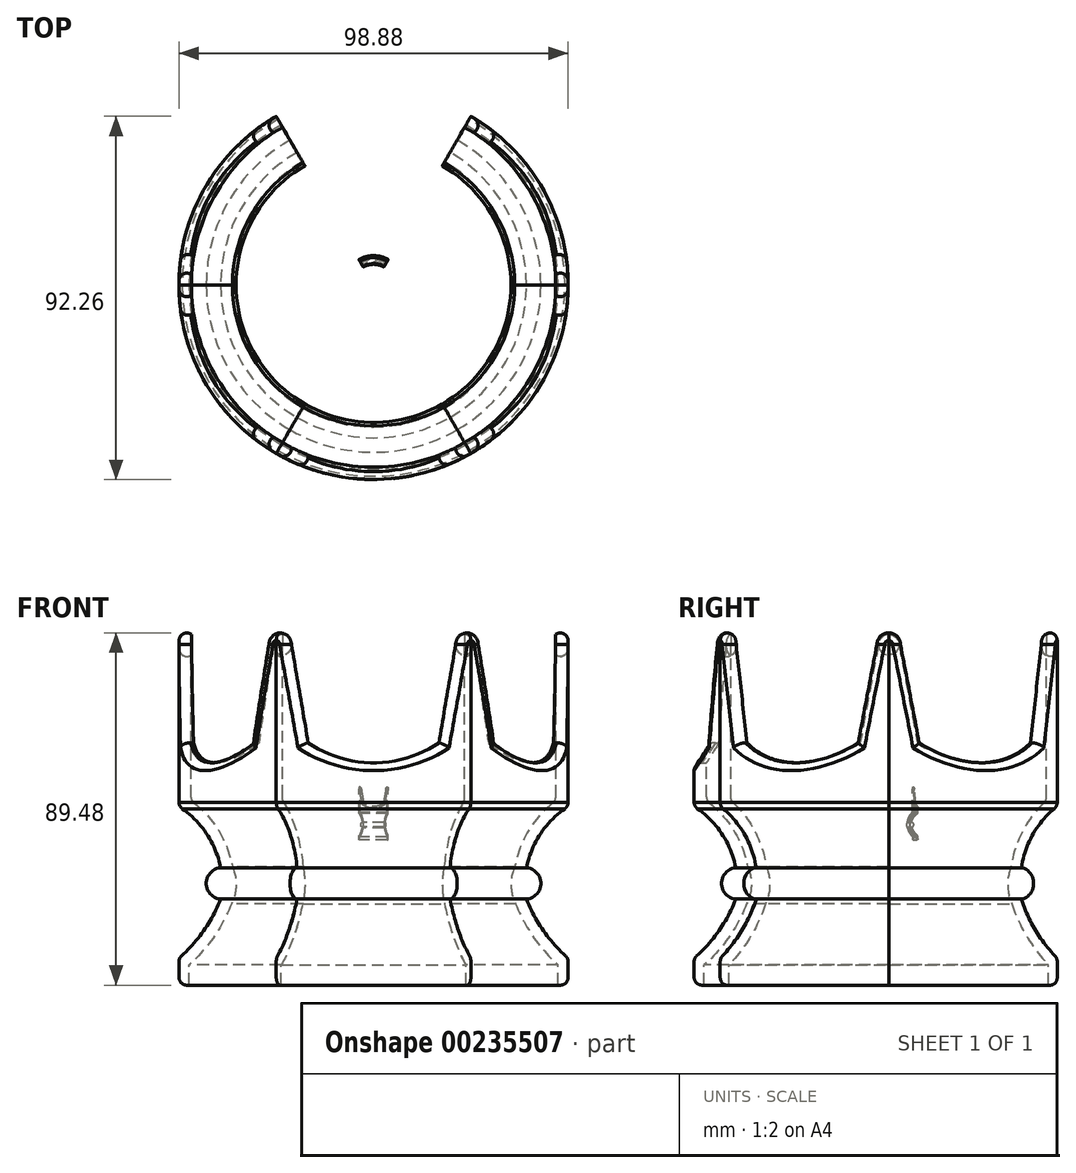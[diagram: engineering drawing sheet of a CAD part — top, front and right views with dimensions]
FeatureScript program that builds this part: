
annotation { "Feature Type Name" : "Feature", "Feature Type Description" : "" }
export const myFeature = defineFeature(function(context is Context, id is Id, definition is map)
    precondition{}
    {
        {
            var Q0;
            Q0=qCreatedBy(makeId("Front.planeOp"),FACE);
            var sketch = newSketch(context, id + "F0", { "sketchPlane" : qUnion([Q0])});
            skLineSegment(sketch, "E0", {"start": v(49.44, 43.1) * mm, "end": v(49.44, 3.07) * mm});
            skArc(sketch, "E1", {"start": v(48.6, 1.43) * mm, "mid": v(42.28, -5.13) * mm, "end": v(38.86, -13.57) * mm});
            skArc(sketch, "E2", {"start": v(38.86, -21.54) * mm, "mid": v(42.5, -17.55) * mm, "end": v(38.86, -13.57) * mm});
            skArc(sketch, "E3", {"start": v(38.86, -21.54) * mm, "mid": v(42.97, -29.33) * mm, "end": v(48.78, -35.95) * mm});
            skLineSegment(sketch, "E4", {"start": v(49.44, -37.44) * mm, "end": v(49.44, -41.4) * mm});
            skPoint(sketch, "E5.visualSharp", {"position": v(49.44, -36.54) * mm});
            skArc(sketch, "E5.filletArc", {"start": v(49.44, -37.44) * mm, "mid": v(49.27, -36.63) * mm, "end": v(48.78, -35.95) * mm});
            skPoint(sketch, "E6.visualSharp", {"position": v(49.44, -43.4) * mm});
            skArc(sketch, "E6.filletArc", {"start": v(46.88, -43.32) * mm, "mid": v(48.64, -43) * mm, "end": v(49.44, -41.4) * mm});
            skPoint(sketch, "E7.visualSharp", {"position": v(49.44, 3.1) * mm});
            skArc(sketch, "E7.filletArc", {"start": v(48.6, 1.43) * mm, "mid": v(49.21, 2.15) * mm, "end": v(49.44, 3.07) * mm});
            skArc(sketch, "E8.0", {"start": v(36.1, -22.7) * mm, "mid": v(40.57, -31.13) * mm, "end": v(46.88, -38.28) * mm});
            skLineSegment(sketch, "E9", {"start": v(46.88, -38.28) * mm, "end": v(46.88, -41.4) * mm});
            skLineSegment(sketch, "E10", {"start": v(46.88, -41.4) * mm, "end": v(46.88, -43.32) * mm});
            skArc(sketch, "E11.0", {"start": v(45.55, 2.9) * mm, "mid": v(39.22, -4.37) * mm, "end": v(35.84, -13.4) * mm});
            skArc(sketch, "E12", {"start": v(35.84, -13.4) * mm, "mid": v(34.92, -18.08) * mm, "end": v(36.1, -22.7) * mm});
            skLineSegment(sketch, "E13", {"start": v(46.3, 4.45) * mm, "end": v(46.3, 43.1) * mm});
            skLineSegment(sketch, "E14", {"start": v(46.3, 43.1) * mm, "end": v(49.44, 43.1) * mm});
            skPoint(sketch, "E15.visualSharp", {"position": v(46.3, 3.47) * mm});
            skArc(sketch, "E15.filletArc", {"start": v(45.55, 2.9) * mm, "mid": v(46.1, 3.59) * mm, "end": v(46.3, 4.45) * mm});
            skLineSegment(sketch, "E16", {"start": v(0, 52.9) * mm, "end": v(0, -29.72) * mm});
            skSolve(sketch);
        }
        {
            var Q0;
            Q0 = qSketchRegion(id + "F0", true);
            var Q1;
            Q1=sQuery(id+"F0.wireOp",EDGE,"E16");
            revolve(context, id + "F1", {"entities" : qUnion([Q0]), "axis" : qUnion([Q1]), "revolveType" : RevolveType.FULL});
        }
        {
            var Q0;
            Q0=qCreatedBy(makeId("Front.planeOp"),FACE);
            var sketch = newSketch(context, id + "F2", { "sketchPlane" : qUnion([Q0])});
            skLineSegment(sketch, "E17", {"start": v(49.44, 43.1) * mm, "end": v(49.44, 3.07) * mm, "construction": true});
            skLineSegment(sketch, "E18", {"start": v(-49.44, 3.07) * mm, "end": v(-49.44, 43.1) * mm, "construction": true});
            skLineSegment(sketch, "E19.0", {"start": v(-20.86, 43.1) * mm, "end": v(20.86, 43.1) * mm});
            skArc(sketch, "E20", {"start": v(-16.58, 18.1) * mm, "mid": v(0, 13.1) * mm, "end": v(16.58, 18.1) * mm});
            skPoint(sketch, "E21.orphan", {"position": v(49.44, 43.1) * mm});
            skPoint(sketch, "E22.orphan", {"position": v(-49.44, 43.1) * mm});
            skLineSegment(sketch, "E23", {"start": v(-20.86, 43.1) * mm, "end": v(-16.58, 18.1) * mm});
            skLineSegment(sketch, "E24", {"start": v(20.86, 43.1) * mm, "end": v(16.58, 18.1) * mm});
            skSolve(sketch);
        }
        {
            var Q0;
            Q0=makeQuery(id+"F2.imprint","IMPRINT",FACE,{"disambiguationData":[TD([[makeQuery(id+"F2.imprint","IMPRINT",EDGE,{"derivedFrom":sQuery(id+"F2.wireOp",EDGE,"E19.0")}),-1.0]])]});
            extrude(context, id + "F3", {"entities" : qUnion([Q0]), "operationType" : NewBodyOperationType.REMOVE, "depth" : 88 * mm});
        }
        {
            var Q0;
            Q0=qCreatedBy(makeId("Top.planeOp"),FACE);
            var sketch = newSketch(context, id + "F4", { "sketchPlane" : qUnion([Q0])});
            skLineSegment(sketch, "E25", {"start": v(0, 0) * mm, "end": v(24.72, -42.82) * mm});
            skLineSegment(sketch, "E26", {"start": v(0, 0) * mm, "end": v(-24.72, -42.82) * mm});
            skLineSegment(sketch, "E27", {"start": v(0, 0) * mm, "end": v(0, -66.04) * mm, "construction": true});
            skArc(sketch, "E28.trimOffspring", {"start": v(-24.72, -42.82) * mm, "mid": v(0, -49.44) * mm, "end": v(24.72, -42.82) * mm});
            skCircle(sketch, "E29", {"center": v(0, 0) * mm, "radius": 71.23 * mm});
            skSolve(sketch);
        }
        {
            var Q0;
            Q0=makeQuery(id+"F4.imprint","IMPRINT",FACE,{"disambiguationData":[TD([[makeQuery(id+"F4.imprint","IMPRINT",EDGE,{"derivedFrom":sQuery(id+"F4.wireOp",EDGE,"E25")}),1.0]])]});
            extrude(context, id + "F5", {"entities" : qUnion([Q0]), "operationType" : NewBodyOperationType.REMOVE, "endBound" : BoundingType.THROUGH_ALL, "oppositeDirection" : true, "depth" : 25 * mm, "hasSecondDirection" : true, "secondDirectionBound" : SecondDirectionBoundingType.THROUGH_ALL, "secondDirectionOppositeDirection" : false, "secondDirectionDepth" : 25 * mm});
        }
        {
            var Q0;
            Q0=makeQuery(id+"F3.boolean.opBoolean","INTERSECT",EDGE,{"derivedFrom":[makeQuery(id+"F1.opRevolve","SWEPT_FACE",FACE,{"disambiguationData":[OSD([sQuery(id+"F0.wireOp",EDGE,"E0")])]}),makeQuery(id+"F3.opExtrude","SWEPT_FACE",FACE,{"disambiguationData":[OSD([sQuery(id+"F2.wireOp",EDGE,"E24")])]})]});
            var Q1;
            Q1=makeQuery(id+"F3.boolean.opBoolean","INTERSECT",EDGE,{"derivedFrom":[makeQuery(id+"F1.opRevolve","SWEPT_FACE",FACE,{"disambiguationData":[OSD([sQuery(id+"F0.wireOp",EDGE,"E0")])]}),makeQuery(id+"F3.opExtrude","SWEPT_FACE",FACE,{"disambiguationData":[OSD([sQuery(id+"F2.wireOp",EDGE,"E23")])]})]});
            var Q2;
            Q2=makeQuery(id+"F3.boolean.opBoolean","INTERSECT",EDGE,{"derivedFrom":[makeQuery(id+"F1.opRevolve","SWEPT_FACE",FACE,{"disambiguationData":[OSD([sQuery(id+"F0.wireOp",EDGE,"E0")])]}),makeQuery(id+"F3.opExtrude","SWEPT_FACE",FACE,{"disambiguationData":[OSD([sQuery(id+"F2.wireOp",EDGE,"E20")])]})]});
            fillet(context, id + "F6", {"entities" : qUnion([Q0, Q1, Q2]), "radius" : 2 * mm, "tangentPropagation" : true, "allowEdgeOverflow" : false});
        }
        {
            var Q0;
            Q0=makeQuery(id+"F5.boolean.opBoolean","SPLIT",FACE,{"disambiguationData":[TD([makeQuery(id+"F3.boolean.opBoolean","COPY",FACE,{"derivedFrom":makeQuery(id+"F3.opExtrude","SWEPT_FACE",FACE,{"disambiguationData":[OSD([sQuery(id+"F2.wireOp",EDGE,"E24")])]})})])],"derivedFrom":makeQuery(id+"F1.opRevolve","SWEPT_FACE",FACE,{"disambiguationData":[OSD([sQuery(id+"F0.wireOp",EDGE,"E14")])]})});
            var sketch = newSketch(context, id + "F7", { "sketchPlane" : qUnion([Q0])});
            skArc(sketch, "E30.0", {"start": v(20.86, -41.33) * mm, "mid": v(22.01, -40.73) * mm, "end": v(23.15, -40.1) * mm});
            skFitSpline(sketch, "E30.1", {"points": [v(20.86, -41.58) * mm, v(20.86, -41.76) * mm, v(20.9, -42.02) * mm, v(21, -42.35) * mm, v(21.16, -42.66) * mm, v(21.38, -42.94) * mm, v(21.64, -43.16) * mm, v(21.93, -43.35) * mm, v(22.25, -43.48) * mm, v(22.6, -43.55) * mm, v(22.94, -43.57) * mm, v(23.37, -43.52) * mm, v(23.7, -43.39) * mm, v(23.85, -43.3) * mm]});
            skPoint(sketch, "E30.2", {"position": v(23.93, -41.45) * mm});
            skLineSegment(sketch, "E31.0.0", {"start": v(20.86, -41.33) * mm, "end": v(20.86, -41.58) * mm, "construction": true});
            skFitSpline(sketch, "E31.0.1", {"points": [v(20.86, -41.58) * mm, v(20.86, -41.76) * mm, v(20.9, -42.02) * mm, v(21, -42.35) * mm, v(21.16, -42.66) * mm, v(21.38, -42.94) * mm, v(21.64, -43.16) * mm, v(21.93, -43.35) * mm, v(22.25, -43.48) * mm, v(22.6, -43.55) * mm, v(22.94, -43.57) * mm, v(23.37, -43.52) * mm, v(23.7, -43.39) * mm, v(23.85, -43.3) * mm], "construction": true});
            skArc(sketch, "E31.0.2", {"start": v(23.85, -43.3) * mm, "mid": v(24.29, -43.06) * mm, "end": v(24.72, -42.82) * mm, "construction": true});
            skLineSegment(sketch, "E31.0.3", {"start": v(24.72, -42.82) * mm, "end": v(23.15, -40.1) * mm, "construction": true});
            skArc(sketch, "E31.0.4", {"start": v(23.15, -40.1) * mm, "mid": v(22.01, -40.73) * mm, "end": v(20.86, -41.33) * mm, "construction": true});
            skLineSegment(sketch, "E32.0.0", {"start": v(20.86, -41.33) * mm, "end": v(20.86, -41.58) * mm});
            skFitSpline(sketch, "E32.0.1", {"points": [v(20.86, -41.58) * mm, v(20.86, -41.76) * mm, v(20.9, -42.02) * mm, v(21, -42.35) * mm, v(21.16, -42.66) * mm, v(21.38, -42.94) * mm, v(21.64, -43.16) * mm, v(21.93, -43.35) * mm, v(22.25, -43.48) * mm, v(22.6, -43.55) * mm, v(22.94, -43.57) * mm, v(23.37, -43.52) * mm, v(23.7, -43.39) * mm, v(23.85, -43.3) * mm]});
            skArc(sketch, "E32.0.2", {"start": v(23.85, -43.3) * mm, "mid": v(24.29, -43.06) * mm, "end": v(24.72, -42.82) * mm});
            skLineSegment(sketch, "E32.0.3", {"start": v(24.72, -42.82) * mm, "end": v(23.15, -40.1) * mm});
            skArc(sketch, "E32.0.4", {"start": v(23.15, -40.1) * mm, "mid": v(22.01, -40.73) * mm, "end": v(20.86, -41.33) * mm});
            skLineSegment(sketch, "E33", {"start": v(23.15, -40.1) * mm, "end": v(21.3, -36.9) * mm});
            skLineSegment(sketch, "E34", {"start": v(24.72, -42.82) * mm, "end": v(26.3, -45.57) * mm});
            skArc(sketch, "E35", {"start": v(21.3, -36.9) * mm, "mid": v(20.77, -43) * mm, "end": v(26.3, -45.57) * mm});
            skLineSegment(sketch, "E36", {"start": v(21.08, -36.5) * mm, "end": v(27.11, -46.95) * mm});
            skSolve(sketch);
        }
        {
            var Q0;
            Q0=makeQuery(id+"F7.imprint","IMPRINT",FACE,{"disambiguationData":[TD([[makeQuery(id+"F7.imprint","IMPRINT",EDGE,{"derivedFrom":sQuery(id+"F7.wireOp",EDGE,"E32.0.0")}),1.0]])]});
            var Q1;
            Q1=makeQuery(id+"F7.imprint","IMPRINT",FACE,{"disambiguationData":[TD([[makeQuery(id+"F7.imprint","IMPRINT",EDGE,{"derivedFrom":sQuery(id+"F7.wireOp",EDGE,"E32.0.0")}),-1.0]])]});
            var Q2;
            Q2=sQuery(id+"F7.wireOp",EDGE,"E33");
            revolve(context, id + "F8", {"operationType" : NewBodyOperationType.ADD, "entities" : qUnion([Q0, Q1]), "axis" : qUnion([Q2]), "revolveType" : RevolveType.TWO_DIRECTIONS, "angle" : 90 * degree, "angleBack" : 270 * degree});
        }
        {
            var Q0;
            Q0=makeQuery(id+"F1.opRevolve","SWEPT_BODY",BODY,{"disambiguationData":[OSD([sQuery(id+"F0.wireOp",EDGE,"E0"),sQuery(id+"F0.wireOp",EDGE,"E1"),sQuery(id+"F0.wireOp",EDGE,"E2"),sQuery(id+"F0.wireOp",EDGE,"E3"),sQuery(id+"F0.wireOp",EDGE,"E4"),sQuery(id+"F0.wireOp",EDGE,"E5.filletArc"),sQuery(id+"F0.wireOp",EDGE,"E6.filletArc"),sQuery(id+"F0.wireOp",EDGE,"E7.filletArc"),sQuery(id+"F0.wireOp",EDGE,"E8.0"),sQuery(id+"F0.wireOp",EDGE,"E9"),sQuery(id+"F0.wireOp",EDGE,"E10"),sQuery(id+"F0.wireOp",EDGE,"E11.0"),sQuery(id+"F0.wireOp",EDGE,"E12"),sQuery(id+"F0.wireOp",EDGE,"E13"),sQuery(id+"F0.wireOp",EDGE,"E14"),sQuery(id+"F0.wireOp",EDGE,"E15.filletArc")])]});
            var Q1;
            Q1=qCreatedBy(makeId("Right.planeOp"),FACE);
            mirror(context, id + "F9", {"operationType" : NewBodyOperationType.ADD, "entities" : qUnion([Q0]), "mirrorPlane" : qUnion([Q1])});
        }
        {
            var Q0;
            Q0=qCreatedBy(makeId("Front.planeOp"),FACE);
            var sketch = newSketch(context, id + "F10", { "sketchPlane" : qUnion([Q0])});
            skLineSegment(sketch, "E37", {"start": v(0, 0) * mm, "end": v(0, -106.6) * mm, "construction": true});
            skSolve(sketch);
        }
        {
            var Q0;
            Q0=makeQuery(id+"F1.opRevolve","SWEPT_BODY",BODY,{"disambiguationData":[OSD([sQuery(id+"F0.wireOp",EDGE,"E0"),sQuery(id+"F0.wireOp",EDGE,"E1"),sQuery(id+"F0.wireOp",EDGE,"E2"),sQuery(id+"F0.wireOp",EDGE,"E3"),sQuery(id+"F0.wireOp",EDGE,"E4"),sQuery(id+"F0.wireOp",EDGE,"E5.filletArc"),sQuery(id+"F0.wireOp",EDGE,"E6.filletArc"),sQuery(id+"F0.wireOp",EDGE,"E7.filletArc"),sQuery(id+"F0.wireOp",EDGE,"E8.0"),sQuery(id+"F0.wireOp",EDGE,"E9"),sQuery(id+"F0.wireOp",EDGE,"E10"),sQuery(id+"F0.wireOp",EDGE,"E11.0"),sQuery(id+"F0.wireOp",EDGE,"E12"),sQuery(id+"F0.wireOp",EDGE,"E13"),sQuery(id+"F0.wireOp",EDGE,"E14"),sQuery(id+"F0.wireOp",EDGE,"E15.filletArc")])]});
            var Q1;
            Q1=sQuery(id+"F10.wireOp",EDGE,"E37");
            circularPattern(context, id + "F11", {"entities" : qUnion([Q0]), "axis" : qUnion([Q1]), "angle" : 360 * degree, "instanceCount" : 6, "equalSpace" : true});
        }
        {
            var Q0;
            Q0=makeQuery(id+"F11.opPattern","COPY",BODY,{"derivedFrom":makeQuery(id+"F1.opRevolve","SWEPT_BODY",BODY,{"disambiguationData":[OSD([sQuery(id+"F0.wireOp",EDGE,"E0"),sQuery(id+"F0.wireOp",EDGE,"E1"),sQuery(id+"F0.wireOp",EDGE,"E2"),sQuery(id+"F0.wireOp",EDGE,"E3"),sQuery(id+"F0.wireOp",EDGE,"E4"),sQuery(id+"F0.wireOp",EDGE,"E5.filletArc"),sQuery(id+"F0.wireOp",EDGE,"E6.filletArc"),sQuery(id+"F0.wireOp",EDGE,"E7.filletArc"),sQuery(id+"F0.wireOp",EDGE,"E8.0"),sQuery(id+"F0.wireOp",EDGE,"E9"),sQuery(id+"F0.wireOp",EDGE,"E10"),sQuery(id+"F0.wireOp",EDGE,"E11.0"),sQuery(id+"F0.wireOp",EDGE,"E12"),sQuery(id+"F0.wireOp",EDGE,"E13"),sQuery(id+"F0.wireOp",EDGE,"E14"),sQuery(id+"F0.wireOp",EDGE,"E15.filletArc")])]}),"instanceName":"3"});
            var Q1;
            Q1=qCreatedBy(makeId("Origin.pointOp"),VERTEX);
            transform(context, id + "F12", {"entities" : qUnion([Q0]), "transformType" : TransformType.SCALE_UNIFORMLY, "scale" : 0.3, "scalePoint" : qUnion([Q1]), "makeCopy" : false});
        }
        {
            var Q0;
            Q0=makeQuery(id+"F11.opPattern","COPY",BODY,{"derivedFrom":makeQuery(id+"F1.opRevolve","SWEPT_BODY",BODY,{"disambiguationData":[OSD([sQuery(id+"F0.wireOp",EDGE,"E0"),sQuery(id+"F0.wireOp",EDGE,"E1"),sQuery(id+"F0.wireOp",EDGE,"E2"),sQuery(id+"F0.wireOp",EDGE,"E3"),sQuery(id+"F0.wireOp",EDGE,"E4"),sQuery(id+"F0.wireOp",EDGE,"E5.filletArc"),sQuery(id+"F0.wireOp",EDGE,"E6.filletArc"),sQuery(id+"F0.wireOp",EDGE,"E7.filletArc"),sQuery(id+"F0.wireOp",EDGE,"E8.0"),sQuery(id+"F0.wireOp",EDGE,"E9"),sQuery(id+"F0.wireOp",EDGE,"E10"),sQuery(id+"F0.wireOp",EDGE,"E11.0"),sQuery(id+"F0.wireOp",EDGE,"E12"),sQuery(id+"F0.wireOp",EDGE,"E13"),sQuery(id+"F0.wireOp",EDGE,"E14"),sQuery(id+"F0.wireOp",EDGE,"E15.filletArc")])]}),"instanceName":"3"});
            var Q1;
            Q1=qCreatedBy(makeId("Origin.pointOp"),VERTEX);
            transform(context, id + "F13", {"entities" : qUnion([Q0]), "transformType" : TransformType.SCALE_UNIFORMLY, "scale" : 0.5, "scalePoint" : qUnion([Q1]), "makeCopy" : false});
        }
    });
